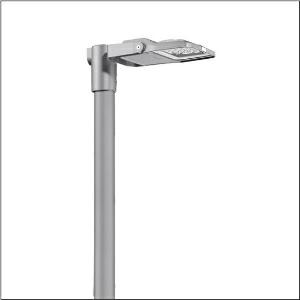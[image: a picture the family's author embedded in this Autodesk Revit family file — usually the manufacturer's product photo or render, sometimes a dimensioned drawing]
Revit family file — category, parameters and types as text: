
# Revit family: floodlight_fl_21_iq_micro___pl33t_5xa7762a2f3a_98d7
name_source: partatom
category: Lighting Fixtures
units: mm (PartAtom-declared; Revit-internal decimal feet)

## family parameters
Cut with Voids When Loaded = No
Host = Face
Light Source = No
Part Type = Normal
Room Calculation Point = No
Round Connector Dimension = Use Diameter
Shared = No

## types (1)
- --- (1 x LED, 2930 lm, 23.1 W, 3000K)
    Apparent Load = 23 VA
    CIE Flux Codes = 26 75 99 100 100
    Color Rendering = 70
    Color Temperature = 3000K
    Default Elevation = 1800 mm
    Description = Floodlight FL 21 iQ micro, floodlight, primary light control with lens, of PMMA, primary optical cover: protective disc, of toughened safety glass, transparent, light distribution: PL33T, light emission: direct distribution, installation type: surface-mounted, LED, High Power LED, rated luminous flux: 2.930lm, luminous efficacy: 127lm/W, light colour: 730, colour temperature: 3000K, control: Auto-Match, Temp-Guard, Night-Set, Smart-Wire, Desk-Remote (wireless, voltage-free reading and setting of iQ features in the workshop via application-optimized NFC function/RFID function), optimised constant luminous flux control (CLO 2.0), Street-Remote, with terminal, 6-pole, mains connection: 220..240V, AC, 50/60Hz, start of lifetime: 23W, end of service life: 24W, reduction: 11W, luminaire housing, of diecast aluminium, powder-coated, Siteco® metallic grey (DB 702S), corrosivity category C5 mid according to DIN EN ISO 12944, sealing non-destructively replaceable, please order mast flange separately, mast bracket, of steel, galvanised, powder-coated, Siteco® metallic grey (DB 702S), protection rating (complete): IP66, insulation class (complete): insulation class II (safety insulation), certification: CE, ENEC, VDE, protection symbol: D, impact resistance: IK07, permissible operating ambient temperature: -40..+40°C, permissible operating ambient temperature for outdoor applications: -40..+50°C, standard: DIN EN 12944, LABS conformity tested according to VDMA 24364:2018-05, packaging unit: 1 piece

Light Distribution: PL33T
    Height = 65 mm
    Lamp = 1 x LED
    Lamp Light Flux = 2930 lm
    Lamp Power = 23.1 W
    Lamp count = 1
    Length = 312 mm
    Luminous efficacy = 127 lm/W
    Manufacturer = Siteco
    ModVariant = No
    Model = 5XA7762A2F3A
    Number of Poles = 1
    OnlyDefault = Yes
    Power Factor = 1
    Product Name = Floodlight FL 21 iQ micro | PL33T
    Product group = floodlight | pylon annexe
    ProductGroupID = 6200
    Protection Class = Protection class II
    Protection Degree = IP 66
    RLX_Detail_Level = 1
    RLX_Emergency_Light_Flux = 0 lm
    RLX_Emergency_Type = 0
    RLX_Emergency_Type_DB = No
    RlxData = <blob elided: 101521 chars, md5=41dc336c>
    Socket = socket
    Standby Power = 0 W
    System Light Flux = 2930 lm
    System Power = 23 W
    Type Comments = factory setting: luminous flux: 100 % | dim-lin: 254 | 455 mA
    Type Image = l_1007121.jpg
    URL = http://relux.com
    VarID = @adj_080457
    Voltage = 0 V
    Weight = 0.00 kg
    Width = 230 mm

## geometry (parser evidence)
native form markers: Blend x4, Sweep x12
no freeform markers — native parametric forms only
